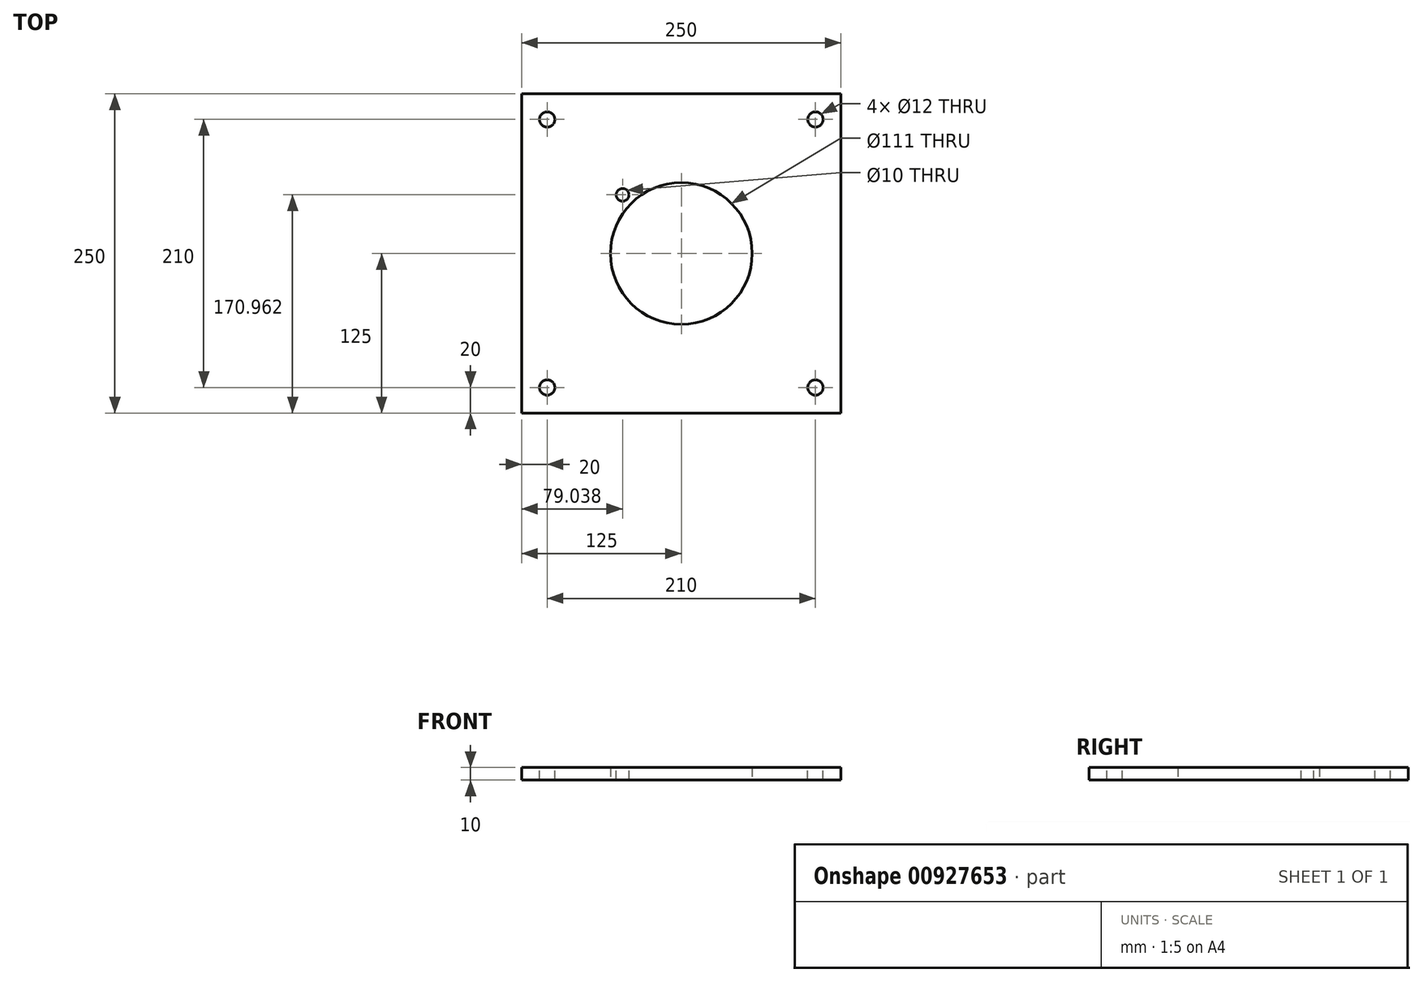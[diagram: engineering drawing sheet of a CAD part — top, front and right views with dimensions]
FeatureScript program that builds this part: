
annotation { "Feature Type Name" : "Feature", "Feature Type Description" : "" }
export const myFeature = defineFeature(function(context is Context, id is Id, definition is map)
    precondition{}
    {
        {
            var Q0;
            Q0=qCreatedBy(makeId("Top.planeOp"),FACE);
            var sketch = newSketch(context, id + "F0", { "sketchPlane" : qUnion([Q0])});
            skLineSegment(sketch, "E0.bottom", {"start": v(125, 125) * mm, "end": v(-125, 125) * mm});
            skLineSegment(sketch, "E0.top", {"start": v(125, -125) * mm, "end": v(-125, -125) * mm});
            skLineSegment(sketch, "E0.left", {"start": v(125, 125) * mm, "end": v(125, -125) * mm});
            skLineSegment(sketch, "E0.right", {"start": v(-125, 125) * mm, "end": v(-125, -125) * mm});
            skPoint(sketch, "E0.middle", {"position": v(0, 0) * mm});
            skCircle(sketch, "E1", {"center": v(0, 0) * mm, "radius": 55.5 * mm});
            skSolve(sketch);
        }
        {
            var Q0;
            Q0 = qSketchRegion(id + "F0", true);
            extrude(context, id + "F1", {"entities" : qUnion([Q0]), "depth" : 10 * mm, "offsetDistance" : 25 * mm});
        }
        {
            var Q0;
            Q0=makeQuery(id+"F1.opExtrude","CAP_FACE",FACE,{"disambiguationData":[OSD([sQuery(id+"F0.wireOp",EDGE,"E0.bottom"),sQuery(id+"F0.wireOp",EDGE,"E0.top"),sQuery(id+"F0.wireOp",EDGE,"E0.left"),sQuery(id+"F0.wireOp",EDGE,"E0.right"),sQuery(id+"F0.wireOp",EDGE,"E1")])],"isStart":false});
            var sketch = newSketch(context, id + "F2", { "sketchPlane" : qUnion([Q0])});
            skCircle(sketch, "E2", {"center": v(0, 0) * mm, "radius": 65 * mm, "construction": true});
            skLineSegment(sketch, "E3", {"start": v(0, 125) * mm, "end": v(0, 0) * mm, "construction": true});
            skLineSegment(sketch, "E4", {"start": v(0, 0) * mm, "end": v(-45.96, 45.96) * mm, "construction": true});
            skCircle(sketch, "E5", {"center": v(-45.96, 45.96) * mm, "radius": 5 * mm});
            skSolve(sketch);
        }
        {
            var Q0;
            Q0 = qSketchRegion(id + "F2", true);
            extrude(context, id + "F3", {"entities" : qUnion([Q0]), "operationType" : NewBodyOperationType.REMOVE, "oppositeDirection" : true, "depth" : 25 * mm, "offsetDistance" : 25 * mm});
        }
        {
            var Q0;
            Q0=makeQuery(id+"F1.opExtrude","CAP_FACE",FACE,{"disambiguationData":[OSD([sQuery(id+"F0.wireOp",EDGE,"E0.bottom"),sQuery(id+"F0.wireOp",EDGE,"E0.top"),sQuery(id+"F0.wireOp",EDGE,"E0.left"),sQuery(id+"F0.wireOp",EDGE,"E0.right"),sQuery(id+"F0.wireOp",EDGE,"E1")])],"isStart":false});
            var sketch = newSketch(context, id + "F4", { "sketchPlane" : qUnion([Q0])});
            skLineSegment(sketch, "E6.bottom", {"start": v(105, 105) * mm, "end": v(-105, 105) * mm, "construction": true});
            skLineSegment(sketch, "E6.top", {"start": v(105, -105) * mm, "end": v(-105, -105) * mm, "construction": true});
            skLineSegment(sketch, "E6.left", {"start": v(105, 105) * mm, "end": v(105, -105) * mm, "construction": true});
            skLineSegment(sketch, "E6.right", {"start": v(-105, 105) * mm, "end": v(-105, -105) * mm, "construction": true});
            skPoint(sketch, "E6.middle", {"position": v(0, 0) * mm});
            skCircle(sketch, "E7", {"center": v(-105, 105) * mm, "radius": 6 * mm});
            skCircle(sketch, "E8", {"center": v(105, 105) * mm, "radius": 6 * mm});
            skCircle(sketch, "E9", {"center": v(105, -105) * mm, "radius": 6 * mm});
            skCircle(sketch, "E10", {"center": v(-105, -105) * mm, "radius": 6 * mm});
            skSolve(sketch);
        }
        {
            var Q0;
            Q0 = qSketchRegion(id + "F4", true);
            extrude(context, id + "F5", {"entities" : qUnion([Q0]), "operationType" : NewBodyOperationType.REMOVE, "endBound" : BoundingType.THROUGH_ALL, "oppositeDirection" : true, "depth" : 25 * mm, "offsetDistance" : 25 * mm});
        }
    });
